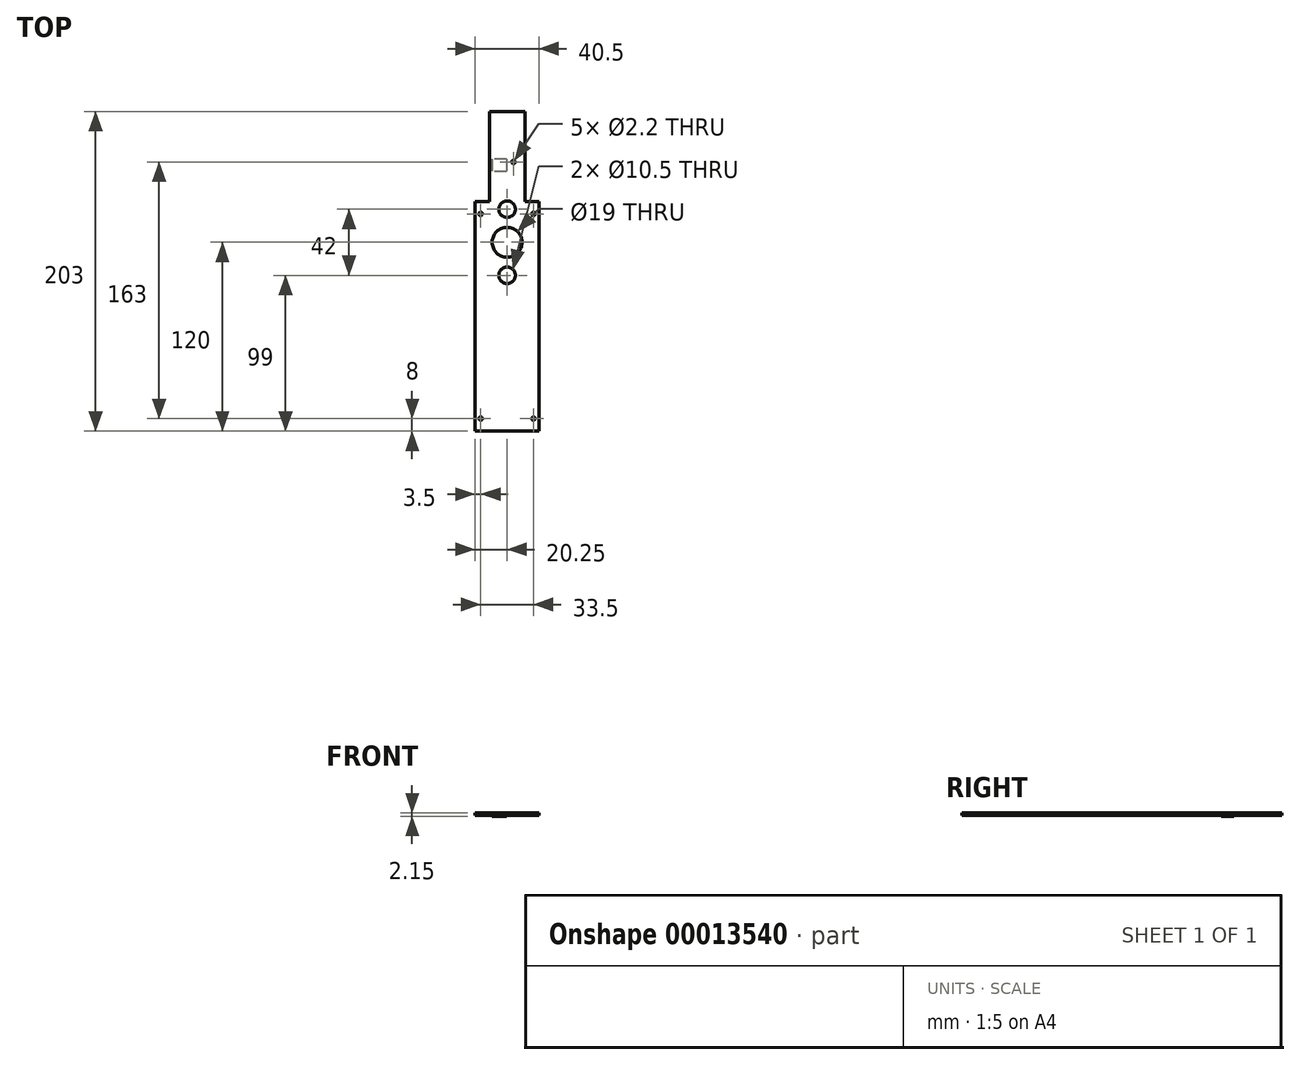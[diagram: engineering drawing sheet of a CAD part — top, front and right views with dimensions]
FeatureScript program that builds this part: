
annotation { "Feature Type Name" : "Feature", "Feature Type Description" : "" }
export const myFeature = defineFeature(function(context is Context, id is Id, definition is map)
    precondition{}
    {
        {
            var Q0;
            Q0=qCreatedBy(makeId("Top.planeOp"),FACE);
            var sketch = newSketch(context, id + "F0", { "sketchPlane" : qUnion([Q0])});
            skLineSegment(sketch, "E0", {"start": v(0, 0) * mm, "end": v(0, 57) * mm});
            skLineSegment(sketch, "E1", {"start": v(0, 57) * mm, "end": v(22.5, 57) * mm});
            skLineSegment(sketch, "E2", {"start": v(22.5, 57) * mm, "end": v(22.5, 0) * mm});
            skLineSegment(sketch, "E3", {"start": v(22.5, 0) * mm, "end": v(31.5, 0) * mm});
            skLineSegment(sketch, "E4", {"start": v(31.5, 0) * mm, "end": v(31.5, -146) * mm});
            skLineSegment(sketch, "E5", {"start": v(31.5, -146) * mm, "end": v(-9, -146) * mm});
            skLineSegment(sketch, "E6", {"start": v(-9, -146) * mm, "end": v(-9, 0) * mm});
            skLineSegment(sketch, "E7", {"start": v(-9, 0) * mm, "end": v(0, 0) * mm});
            skCircle(sketch, "E8", {"center": v(11.25, -26) * mm, "radius": 9.5 * mm});
            skLineSegment(sketch, "E9", {"start": v(11.25, 57) * mm, "end": v(11.25, -146) * mm, "construction": true});
            skCircle(sketch, "E10", {"center": v(15.25, 25) * mm, "radius": 1.1 * mm});
            skCircle(sketch, "E11", {"center": v(-5.5, -8) * mm, "radius": 1.1 * mm});
            skLineSegment(sketch, "E12.rect.bottom", {"start": v(28, -8) * mm, "end": v(-5.5, -8) * mm, "construction": true});
            skLineSegment(sketch, "E12.rect.top", {"start": v(28, -138) * mm, "end": v(-5.5, -138) * mm, "construction": true});
            skLineSegment(sketch, "E12.rect.left", {"start": v(28, -8) * mm, "end": v(28, -138) * mm, "construction": true});
            skLineSegment(sketch, "E12.rect.right", {"start": v(-5.5, -8) * mm, "end": v(-5.5, -138) * mm, "construction": true});
            skPoint(sketch, "E12.rect.middle", {"position": v(11.25, -73) * mm});
            skCircle(sketch, "E13.0.1.0", {"center": v(-5.5, -138) * mm, "radius": 1.1 * mm});
            skCircle(sketch, "E13.1.0.0", {"center": v(28, -8) * mm, "radius": 1.1 * mm});
            skCircle(sketch, "E13.1.1.0", {"center": v(28, -138) * mm, "radius": 1.1 * mm});
            skLineSegment(sketch, "E13.direction1", {"start": v(-5.5, -8) * mm, "end": v(28, -8) * mm, "construction": true});
            skLineSegment(sketch, "E14", {"start": v(28, 2.5) * mm, "end": v(28, -146) * mm, "construction": true});
            skLineSegment(sketch, "E15", {"start": v(23.5, 2.5) * mm, "end": v(32.5, 2.5) * mm, "construction": true});
            skLineSegment(sketch, "E16", {"start": v(-1, 2.34) * mm, "end": v(-10, 2.34) * mm, "construction": true});
            skLineSegment(sketch, "E17", {"start": v(-5.5, 2.34) * mm, "end": v(-5.5, -8) * mm, "construction": true});
            skSolve(sketch);
        }
        {
            var Q0;
            Q0 = qSketchRegion(id + "F0", true);
            extrude(context, id + "F1", {"entities" : qUnion([Q0]), "depth" : 1.67 * mm});
        }
        {
            var Q0;
            Q0=qCreatedBy(makeId("Top.planeOp"),FACE);
            var sketch = newSketch(context, id + "F2", { "sketchPlane" : qUnion([Q0])});
            skLineSegment(sketch, "E18", {"start": v(11.25, -26) * mm, "end": v(11.25, -146) * mm, "construction": true});
            skLineSegment(sketch, "E19", {"start": v(11.25, -26) * mm, "end": v(11.25, 57) * mm, "construction": true});
            skCircle(sketch, "E20", {"center": v(11.25, -47) * mm, "radius": 5.25 * mm});
            skCircle(sketch, "E21", {"center": v(11.25, -5) * mm, "radius": 5.25 * mm});
            skLineSegment(sketch, "E22", {"start": v(11.25, -5) * mm, "end": v(11.25, -26) * mm, "construction": true});
            skLineSegment(sketch, "E23", {"start": v(11.25, -26) * mm, "end": v(11.25, -47) * mm, "construction": true});
            skSolve(sketch);
        }
        {
            var Q0;
            Q0=makeQuery(id+"F2.imprint","IMPRINT",FACE,{"disambiguationData":[TD([[makeQuery(id+"F2.imprint","IMPRINT",EDGE,{"derivedFrom":sQuery(id+"F2.wireOp",EDGE,"E21")}),1.0]])]});
            var Q1;
            Q1=makeQuery(id+"F2.imprint","IMPRINT",FACE,{"disambiguationData":[TD([[makeQuery(id+"F2.imprint","IMPRINT",EDGE,{"derivedFrom":sQuery(id+"F2.wireOp",EDGE,"E20")}),1.0]])]});
            var Q2;
            Q2=makeQuery(id+"F1.opExtrude","CAP_FACE",FACE,{"disambiguationData":[OSD([sQuery(id+"F0.wireOp",EDGE,"E0"),sQuery(id+"F0.wireOp",EDGE,"E1"),sQuery(id+"F0.wireOp",EDGE,"E2"),sQuery(id+"F0.wireOp",EDGE,"E3"),sQuery(id+"F0.wireOp",EDGE,"E4"),sQuery(id+"F0.wireOp",EDGE,"E5"),sQuery(id+"F0.wireOp",EDGE,"E6"),sQuery(id+"F0.wireOp",EDGE,"E7"),sQuery(id+"F0.wireOp",EDGE,"E8"),sQuery(id+"F0.wireOp",EDGE,"E10"),sQuery(id+"F0.wireOp",EDGE,"E11"),sQuery(id+"F0.wireOp",EDGE,"E13.0.1.0"),sQuery(id+"F0.wireOp",EDGE,"E13.1.0.0"),sQuery(id+"F0.wireOp",EDGE,"E13.1.1.0")])],"isStart":false});
            extrude(context, id + "F3", {"entities" : qUnion([Q0, Q1]), "operationType" : NewBodyOperationType.REMOVE, "endBound" : BoundingType.THROUGH_ALL, "endBoundEntityFace" : qUnion([Q2]), "depth" : 25 * mm});
        }
        {
            var Q0;
            Q0=makeQuery(id+"F1.opExtrude","CAP_FACE",FACE,{"disambiguationData":[OSD([sQuery(id+"F0.wireOp",EDGE,"E0"),sQuery(id+"F0.wireOp",EDGE,"E1"),sQuery(id+"F0.wireOp",EDGE,"E2"),sQuery(id+"F0.wireOp",EDGE,"E3"),sQuery(id+"F0.wireOp",EDGE,"E4"),sQuery(id+"F0.wireOp",EDGE,"E5"),sQuery(id+"F0.wireOp",EDGE,"E6"),sQuery(id+"F0.wireOp",EDGE,"E7"),sQuery(id+"F0.wireOp",EDGE,"E8"),sQuery(id+"F0.wireOp",EDGE,"E10"),sQuery(id+"F0.wireOp",EDGE,"E11"),sQuery(id+"F0.wireOp",EDGE,"E13.0.1.0"),sQuery(id+"F0.wireOp",EDGE,"E13.1.0.0"),sQuery(id+"F0.wireOp",EDGE,"E13.1.1.0")])],"isStart":true});
            var sketch = newSketch(context, id + "F4", { "sketchPlane" : qUnion([Q0])});
            skLineSegment(sketch, "E24.bottom", {"start": v(10.8, -26.77) * mm, "end": v(1.8, -26.77) * mm});
            skLineSegment(sketch, "E24.top", {"start": v(10.8, -18.87) * mm, "end": v(1.8, -18.87) * mm});
            skLineSegment(sketch, "E24.left", {"start": v(10.8, -26.77) * mm, "end": v(10.8, -18.87) * mm});
            skLineSegment(sketch, "E24.right", {"start": v(1.8, -26.77) * mm, "end": v(1.8, -18.87) * mm});
            skSolve(sketch);
        }
        {
            var Q0;
            Q0 = qSketchRegion(id + "F4", true);
            extrude(context, id + "F5", {"entities" : qUnion([Q0]), "operationType" : NewBodyOperationType.ADD, "depth" : .478 * mm});
        }
    });
